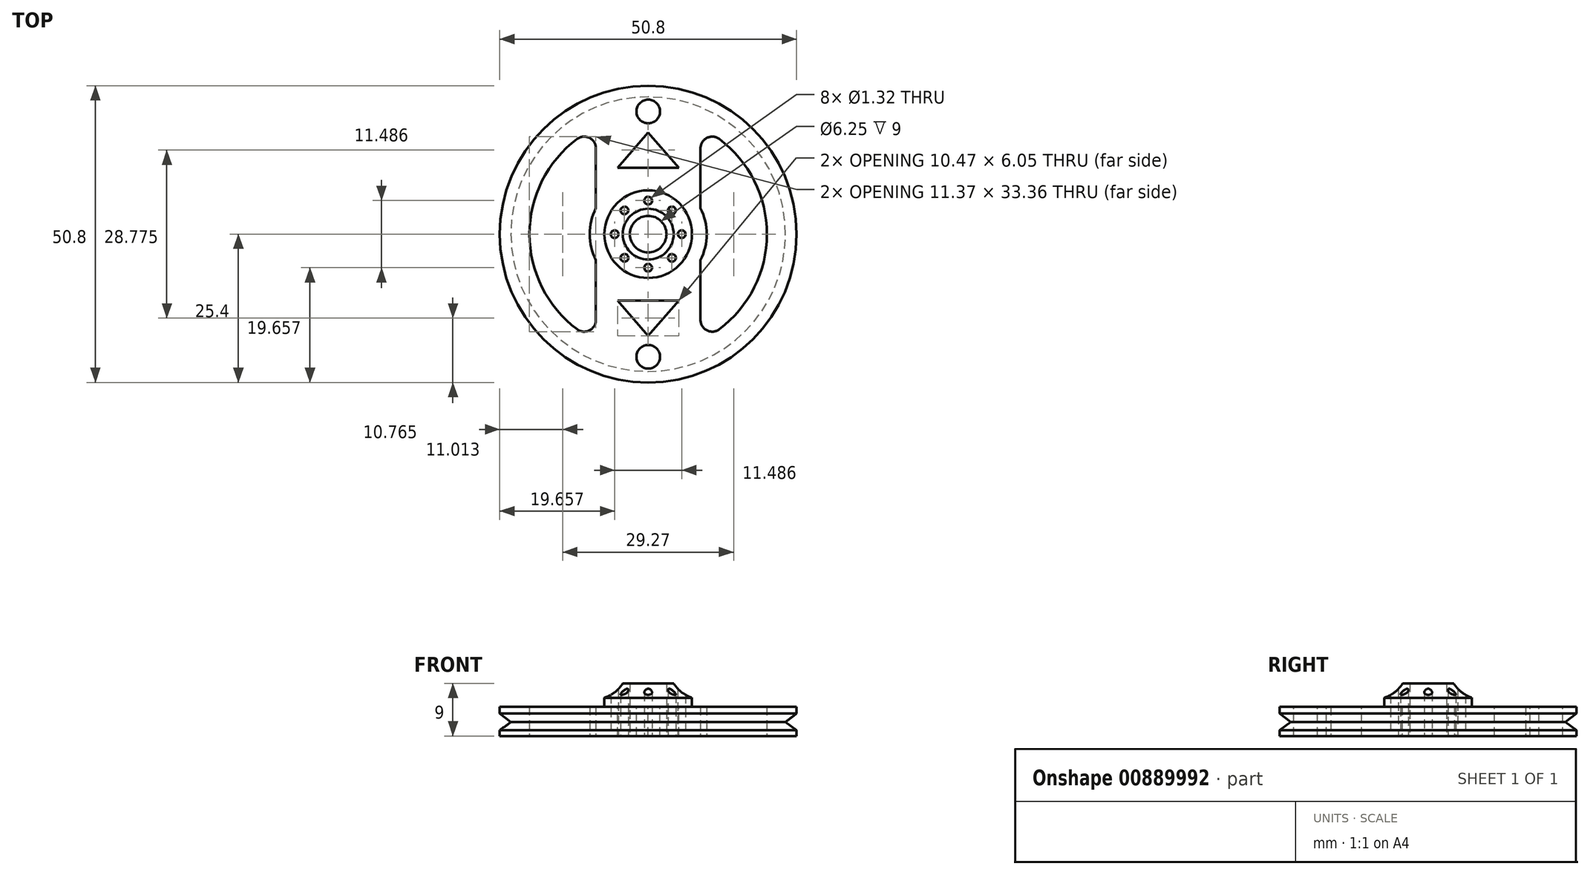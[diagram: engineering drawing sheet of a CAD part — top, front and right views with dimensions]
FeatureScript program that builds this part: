
annotation { "Feature Type Name" : "Feature", "Feature Type Description" : "" }
export const myFeature = defineFeature(function(context is Context, id is Id, definition is map)
    precondition{}
    {
        {
            var Q0;
            Q0=qCreatedBy(makeId("Top.planeOp"),FACE);
            var sketch = newSketch(context, id + "F0", { "sketchPlane" : qUnion([Q0])});
            skCircle(sketch, "E0", {"center": v(0, 0) * mm, "radius": 25.4 * mm});
            skCircle(sketch, "E1", {"center": v(0, 0) * mm, "radius": 3.12 * mm});
            skArc(sketch, "E2", {"start": v(-8.95, 4.46) * mm, "mid": v(-10, 0) * mm, "end": v(-8.95, -4.46) * mm});
            skArc(sketch, "E3.0", {"start": v(-12.15, 16.3) * mm, "mid": v(-20.32, 0) * mm, "end": v(-12.15, -16.3) * mm});
            skLineSegment(sketch, "E4.0", {"start": v(-8.95, 14.69) * mm, "end": v(-8.95, 4.46) * mm});
            skLineSegment(sketch, "E5.0", {"start": v(8.95, 14.69) * mm, "end": v(8.95, 4.46) * mm});
            skPoint(sketch, "E6.orphan", {"position": v(0, 22.46) * mm});
            skPoint(sketch, "E7.visualSharp", {"position": v(-8.95, 18.24) * mm});
            skArc(sketch, "E7.filletArc", {"start": v(-8.95, 14.69) * mm, "mid": v(-10.05, 16.47) * mm, "end": v(-12.15, 16.3) * mm});
            skPoint(sketch, "E8.visualSharp", {"position": v(8.95, 18.24) * mm});
            skArc(sketch, "E8.filletArc", {"start": v(12.15, 16.3) * mm, "mid": v(10.05, 16.47) * mm, "end": v(8.95, 14.69) * mm});
            skArc(sketch, "E9.1.0", {"start": v(-12.15, -16.3) * mm, "mid": v(-10.05, -16.47) * mm, "end": v(-8.95, -14.69) * mm});
            skArc(sketch, "E9.1.1", {"start": v(8.95, -14.69) * mm, "mid": v(10.05, -16.47) * mm, "end": v(12.15, -16.3) * mm});
            skLineSegment(sketch, "E9.1.2", {"start": v(8.95, -14.69) * mm, "end": v(8.95, -4.46) * mm});
            skLineSegment(sketch, "E9.1.3", {"start": v(-8.95, -14.69) * mm, "end": v(-8.95, -4.46) * mm});
            skArc(sketch, "E10.trimOffspring", {"start": v(12.15, -16.3) * mm, "mid": v(20.32, 0) * mm, "end": v(12.15, 16.3) * mm});
            skArc(sketch, "E11.trimOffspring", {"start": v(8.95, -4.46) * mm, "mid": v(10, 0) * mm, "end": v(8.95, 4.46) * mm});
            skSolve(sketch);
        }
        {
            var Q0;
            Q0=makeQuery(id+"F0.imprint","IMPRINT",FACE,{"disambiguationData":[TD([[makeQuery(id+"F0.imprint","IMPRINT",EDGE,{"derivedFrom":sQuery(id+"F0.wireOp",EDGE,"E0")}),1.0]])]});
            extrude(context, id + "F1", {"entities" : qUnion([Q0]), "depth" : 5 * mm, "offsetDistance" : 25.4 * mm});
        }
        {
            var Q0;
            Q0=makeQuery(id+"F1.opExtrude","CAP_FACE",FACE,{"disambiguationData":[OSD([sQuery(id+"F0.wireOp",EDGE,"E0"),sQuery(id+"F0.wireOp",EDGE,"E1"),sQuery(id+"F0.wireOp",EDGE,"E2"),sQuery(id+"F0.wireOp",EDGE,"E3.0"),sQuery(id+"F0.wireOp",EDGE,"E4.0"),sQuery(id+"F0.wireOp",EDGE,"E5.0"),sQuery(id+"F0.wireOp",EDGE,"E7.filletArc"),sQuery(id+"F0.wireOp",EDGE,"E8.filletArc"),sQuery(id+"F0.wireOp",EDGE,"E9.1.0"),sQuery(id+"F0.wireOp",EDGE,"E9.1.1"),sQuery(id+"F0.wireOp",EDGE,"E9.1.2"),sQuery(id+"F0.wireOp",EDGE,"E9.1.3"),sQuery(id+"F0.wireOp",EDGE,"E10.trimOffspring"),sQuery(id+"F0.wireOp",EDGE,"E11.trimOffspring")])],"isStart":false});
            var sketch = newSketch(context, id + "F2", { "sketchPlane" : qUnion([Q0])});
            skCircle(sketch, "E12", {"center": v(0, 0) * mm, "radius": 7.5 * mm});
            skSolve(sketch);
        }
        {
            var Q0;
            Q0=makeQuery(id+"F2.imprint","IMPRINT",FACE,{"disambiguationData":[TD([[makeQuery(id+"F2.imprint","IMPRINT",EDGE,{"derivedFrom":sQuery(id+"F2.wireOp",EDGE,"E12")}),1.0]])]});
            extrude(context, id + "F3", {"entities" : qUnion([Q0]), "operationType" : NewBodyOperationType.ADD, "depth" : 4 * mm, "offsetDistance" : 25.4 * mm});
        }
        {
            var Q0;
            Q0=qCreatedBy(makeId("Front.planeOp"),FACE);
            var sketch = newSketch(context, id + "F4", { "sketchPlane" : qUnion([Q0])});
            skCircle(sketch, "E13", {"center": v(-9.47, 12.31) * mm, "radius": 6.1 * mm});
            skLineSegment(sketch, "E14", {"start": v(0, 13.25) * mm, "end": v(0, -3.15) * mm, "construction": true});
            skSolve(sketch);
        }
        {
            var Q0;
            Q0=makeQuery(id+"F4.imprint","IMPRINT",FACE,{"disambiguationData":[TD([[makeQuery(id+"F4.imprint","IMPRINT",EDGE,{"derivedFrom":sQuery(id+"F4.wireOp",EDGE,"E13")}),1.0]])]});
            var Q1;
            Q1=sQuery(id+"F4.wireOp",EDGE,"E14");
            revolve(context, id + "F5", {"operationType" : NewBodyOperationType.REMOVE, "surfaceOperationType" : NewSurfaceOperationType.NEW, "entities" : qUnion([Q0]), "axis" : qUnion([Q1]), "revolveType" : RevolveType.FULL, "oppositeDirection" : true});
        }
        {
            var Q0;
            Q0=makeQuery(id+"F1.opExtrude","CAP_FACE",FACE,{"disambiguationData":[OSD([sQuery(id+"F0.wireOp",EDGE,"E0"),sQuery(id+"F0.wireOp",EDGE,"E1"),sQuery(id+"F0.wireOp",EDGE,"E2"),sQuery(id+"F0.wireOp",EDGE,"E3.0"),sQuery(id+"F0.wireOp",EDGE,"E4.0"),sQuery(id+"F0.wireOp",EDGE,"E5.0"),sQuery(id+"F0.wireOp",EDGE,"E7.filletArc"),sQuery(id+"F0.wireOp",EDGE,"E8.filletArc"),sQuery(id+"F0.wireOp",EDGE,"E9.1.0"),sQuery(id+"F0.wireOp",EDGE,"E9.1.1"),sQuery(id+"F0.wireOp",EDGE,"E9.1.2"),sQuery(id+"F0.wireOp",EDGE,"E9.1.3"),sQuery(id+"F0.wireOp",EDGE,"E10.trimOffspring"),sQuery(id+"F0.wireOp",EDGE,"E11.trimOffspring")])],"isStart":false});
            var sketch = newSketch(context, id + "F6", { "sketchPlane" : qUnion([Q0])});
            skLineSegment(sketch, "E15", {"start": v(0, 11.36) * mm, "end": v(-5.23, 11.36) * mm});
            skLineSegment(sketch, "E16", {"start": v(-5.23, 11.36) * mm, "end": v(0, 17.41) * mm});
            skLineSegment(sketch, "E17", {"start": v(0, 17.41) * mm, "end": v(0, 11.36) * mm});
            skLineSegment(sketch, "E18.MirrorCS", {"start": v(0, 11.36) * mm, "end": v(5.23, 11.36) * mm});
            skLineSegment(sketch, "E19.MirrorCS", {"start": v(5.23, 11.36) * mm, "end": v(0, 17.41) * mm});
            skLineSegment(sketch, "E20.1.0", {"start": v(-5.23, -11.36) * mm, "end": v(0, -17.41) * mm});
            skLineSegment(sketch, "E20.1.1", {"start": v(5.23, -11.36) * mm, "end": v(0, -17.41) * mm});
            skLineSegment(sketch, "E20.1.2", {"start": v(0, -11.36) * mm, "end": v(-5.23, -11.36) * mm});
            skLineSegment(sketch, "E20.1.3", {"start": v(0, -11.36) * mm, "end": v(5.23, -11.36) * mm});
            skPoint(sketch, "E20.center", {"position": v(0, 0) * mm});
            skCircle(sketch, "E21", {"center": v(0, 21) * mm, "radius": 2.02 * mm});
            skCircle(sketch, "E22.1.0", {"center": v(0, -21) * mm, "radius": 2.02 * mm});
            skSolve(sketch);
        }
        {
            var Q0;
            Q0 = qSketchRegion(id + "F6", true);
            extrude(context, id + "F7", {"entities" : qUnion([Q0]), "operationType" : NewBodyOperationType.REMOVE, "endBound" : BoundingType.THROUGH_ALL, "oppositeDirection" : true, "depth" : 25.4 * mm, "offsetDistance" : 25.4 * mm});
        }
        {
            var Q0;
            Q0=qCreatedBy(makeId("Front.planeOp"),FACE);
            var sketch = newSketch(context, id + "F8", { "sketchPlane" : qUnion([Q0])});
            skLineSegment(sketch, "E23", {"start": v(-25.5, 2.4) * mm, "end": v(-23.5, 2.4) * mm});
            skLineSegment(sketch, "E24", {"start": v(-23.5, 2.4) * mm, "end": v(-25.5, 0.9) * mm});
            skLineSegment(sketch, "E25", {"start": v(-25.5, 0.9) * mm, "end": v(-25.5, 2.4) * mm});
            skLineSegment(sketch, "E26.MirrorCS", {"start": v(-23.5, 2.4) * mm, "end": v(-25.5, 3.9) * mm});
            skLineSegment(sketch, "E27.MirrorCS", {"start": v(-25.5, 3.9) * mm, "end": v(-25.5, 2.4) * mm});
            skLineSegment(sketch, "E28", {"start": v(0, 41.08) * mm, "end": v(0, 0) * mm, "construction": true});
            skSolve(sketch);
        }
        {
            var Q0;
            Q0=qSketchRegion(id+"F8",true);
            var Q1;
            Q1=sQuery(id+"F8.wireOp",EDGE,"E28");
            revolve(context, id + "F9", {"operationType" : NewBodyOperationType.REMOVE, "surfaceOperationType" : NewSurfaceOperationType.NEW, "entities" : qUnion([Q0]), "axis" : qUnion([Q1]), "revolveType" : RevolveType.FULL});
        }
        {
            var Q0;
            Q0=makeQuery(id+"F0.imprint","IMPRINT",FACE,{"disambiguationData":[TD([[makeQuery(id+"F0.imprint","IMPRINT",EDGE,{"derivedFrom":sQuery(id+"F0.wireOp",EDGE,"E5.0")}),1.0]])]});
            var sketch = newSketch(context, id + "F10", { "sketchPlane" : qUnion([Q0])});
            skCircle(sketch, "E29", {"center": v(0, 5.74) * mm, "radius": 0.66 * mm});
            skCircle(sketch, "E30.1.0", {"center": v(-4.06, 4.06) * mm, "radius": 0.66 * mm});
            skCircle(sketch, "E30.2.0", {"center": v(-5.74, 0) * mm, "radius": 0.66 * mm});
            skPoint(sketch, "E30.center", {"position": v(0, 0) * mm});
            skCircle(sketch, "E31.1.3.0", {"center": v(-4.06, -4.06) * mm, "radius": 0.66 * mm});
            skCircle(sketch, "E31.1.4.0", {"center": v(0, -5.74) * mm, "radius": 0.66 * mm});
            skCircle(sketch, "E31.1.5.0", {"center": v(4.06, -4.06) * mm, "radius": 0.66 * mm});
            skCircle(sketch, "E31.1.6.0", {"center": v(5.74, 0) * mm, "radius": 0.66 * mm});
            skCircle(sketch, "E32.1.7.0", {"center": v(4.06, 4.06) * mm, "radius": 0.66 * mm});
            skSolve(sketch);
        }
        {
            var Q0;
            Q0=qSketchRegion(id+"F10",true);
            extrude(context, id + "F11", {"entities" : qUnion([Q0]), "operationType" : NewBodyOperationType.REMOVE, "endBound" : BoundingType.THROUGH_ALL, "depth" : 25.4 * mm, "offsetDistance" : 25.4 * mm});
        }
    });
